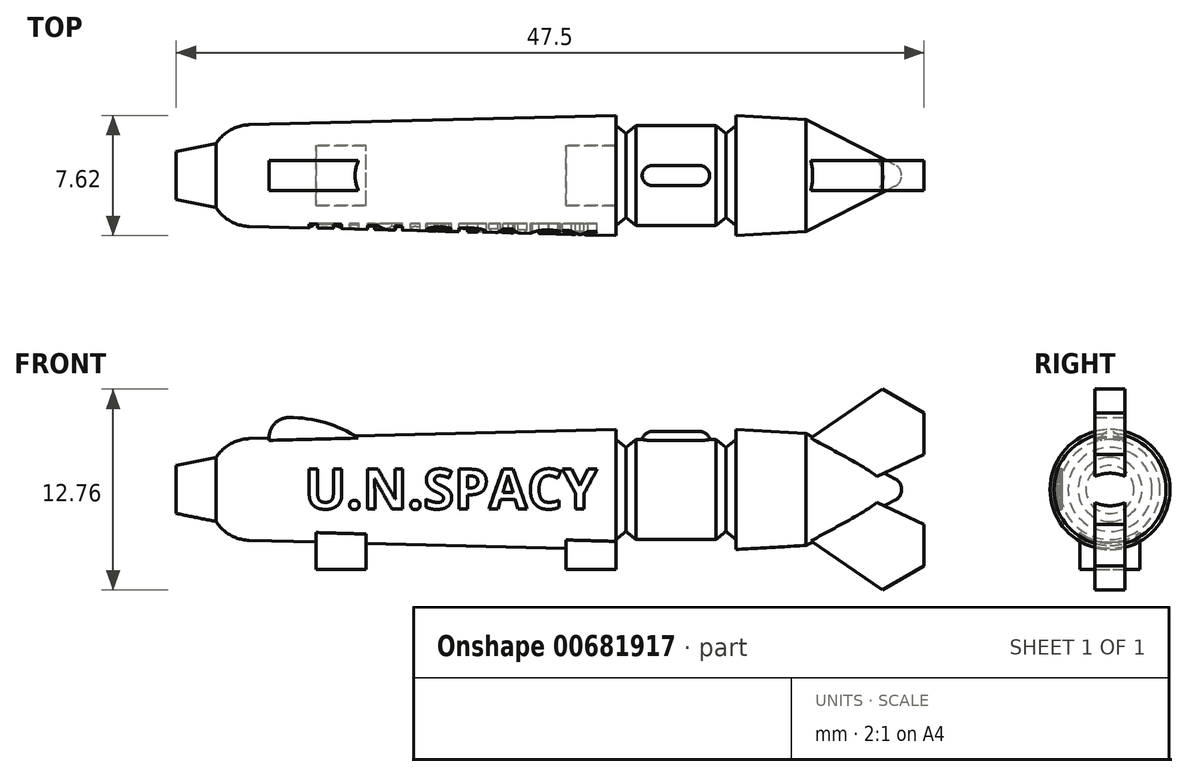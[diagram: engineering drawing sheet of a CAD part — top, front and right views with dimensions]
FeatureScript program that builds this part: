
annotation { "Feature Type Name" : "Feature", "Feature Type Description" : "" }
export const myFeature = defineFeature(function(context is Context, id is Id, definition is map)
    precondition{}
    {
        {
            var Q0;
            Q0=qCreatedBy(makeId("Front.planeOp"),FACE);
            var sketch = newSketch(context, id + "F0", { "sketchPlane" : qUnion([Q0])});
            skLineSegment(sketch, "E0", {"start": v(-36.83, 0) * mm, "end": v(32.69, 0) * mm, "construction": true});
            skLineSegment(sketch, "E1", {"start": v(-27.93, 0) * mm, "end": v(-27.93, 1.52) * mm});
            skLineSegment(sketch, "E2", {"start": v(-27.93, 1.52) * mm, "end": v(-25.4, 2.03) * mm});
            skLineSegment(sketch, "E3", {"start": v(-25.4, 2.03) * mm, "end": v(-25.4, 3.18) * mm});
            skLineSegment(sketch, "E4", {"start": v(-25.4, 3.18) * mm, "end": v(0, 3.81) * mm});
            skLineSegment(sketch, "E5", {"start": v(0, 3.81) * mm, "end": v(0, 3.17) * mm});
            skLineSegment(sketch, "E6", {"start": v(1.27, 3.18) * mm, "end": v(6.35, 3.18) * mm});
            skLineSegment(sketch, "E7", {"start": v(6.99, 2.67) * mm, "end": v(7.62, 3.18) * mm});
            skLineSegment(sketch, "E8", {"start": v(7.62, 3.18) * mm, "end": v(7.62, 3.81) * mm});
            skLineSegment(sketch, "E9", {"start": v(7.62, 3.81) * mm, "end": v(12.07, 3.56) * mm});
            skLineSegment(sketch, "E10", {"start": v(12.07, 3.56) * mm, "end": v(17.73, 0.68) * mm});
            skLineSegment(sketch, "E11", {"start": v(18.14, 0) * mm, "end": v(-27.93, 0) * mm});
            skArc(sketch, "E12", {"start": v(18.14, 0) * mm, "mid": v(18.03, 0.4) * mm, "end": v(17.73, 0.68) * mm});
            skLineSegment(sketch, "E13", {"start": v(6.35, 3.18) * mm, "end": v(6.99, 2.67) * mm});
            skLineSegment(sketch, "E14", {"start": v(3.81, 3.18) * mm, "end": v(3.81, 0) * mm, "construction": true});
            skLineSegment(sketch, "E15.MirrorCS", {"start": v(1.27, 3.18) * mm, "end": v(0.64, 2.67) * mm});
            skLineSegment(sketch, "E16.MirrorCS", {"start": v(0.64, 2.67) * mm, "end": v(0, 3.18) * mm});
            skPoint(sketch, "E17.end.orphan", {"position": v(6.35, 2.16) * mm});
            skPoint(sketch, "E18.orphan", {"position": v(1.27, 2.16) * mm});
            skSolve(sketch);
        }
        {
            var Q0;
            Q0 = qSketchRegion(id + "F0", true);
            var Q1;
            Q1=sQuery(id+"F0.wireOp",EDGE,"E11");
            revolve(context, id + "F1", {"entities" : qUnion([Q0]), "axis" : qUnion([Q1]), "revolveType" : RevolveType.FULL});
        }
        {
            var Q0;
            Q0=makeQuery(id+"F1.opRevolve","SWEPT_EDGE",EDGE,{"disambiguationData":[OSD([sQuery(id+"F0.wireOp",EDGE,"E3"),sQuery(id+"F0.wireOp",EDGE,"E4")])]});
            fillet(context, id + "F2", {"entities" : qUnion([Q0]), "radius" : 2.54 * mm, "allowEdgeOverflow" : false});
        }
        {
            var Q0;
            Q0=qCreatedBy(makeId("Front.planeOp"),FACE);
            var sketch = newSketch(context, id + "F3", { "sketchPlane" : qUnion([Q0])});
            skArc(sketch, "E19", {"start": v(-20.77, 4.57) * mm, "mid": v(-22.03, 3.36) * mm, "end": v(-20.88, 2.04) * mm});
            skArc(sketch, "E20", {"start": v(-14.92, 2.04) * mm, "mid": v(-17.58, 3.92) * mm, "end": v(-20.77, 4.57) * mm});
            skLineSegment(sketch, "E21", {"start": v(-20.88, 2.04) * mm, "end": v(-14.92, 2.04) * mm});
            skPoint(sketch, "E22.orphan", {"position": v(12.68, 0) * mm});
            skLineSegment(sketch, "E23", {"start": v(11.6, 2.73) * mm, "end": v(16.93, 6.38) * mm});
            skLineSegment(sketch, "E24", {"start": v(16.93, 6.38) * mm, "end": v(19.57, 4.86) * mm});
            skLineSegment(sketch, "E25", {"start": v(19.57, 4.86) * mm, "end": v(19.57, 2.23) * mm});
            skLineSegment(sketch, "E26", {"start": v(19.57, 2.23) * mm, "end": v(15.53, 0.34) * mm});
            skLineSegment(sketch, "E27", {"start": v(11.6, 2.73) * mm, "end": v(14.4, 0.34) * mm});
            skLineSegment(sketch, "E28", {"start": v(14.8, 0) * mm, "end": v(12.68, 0) * mm, "construction": true});
            skLineSegment(sketch, "E29.MirrorCS", {"start": v(11.6, -2.73) * mm, "end": v(14.4, -0.34) * mm});
            skLineSegment(sketch, "E30.MirrorCS", {"start": v(11.6, -2.73) * mm, "end": v(16.93, -6.38) * mm});
            skLineSegment(sketch, "E31.MirrorCS", {"start": v(19.57, -4.86) * mm, "end": v(19.57, -2.23) * mm});
            skLineSegment(sketch, "E32.MirrorCS", {"start": v(19.57, -2.23) * mm, "end": v(15.53, -0.34) * mm});
            skLineSegment(sketch, "E33", {"start": v(14.4, 0.34) * mm, "end": v(15.53, 0.34) * mm});
            skPoint(sketch, "E34.MirrorCS.end.orphan", {"position": v(19.57, -4.86) * mm});
            skPoint(sketch, "E34.MirrorCS.start.orphan", {"position": v(16.93, -6.38) * mm});
            skLineSegment(sketch, "E35.MirrorCS", {"start": v(14.4, -0.34) * mm, "end": v(15.53, -0.34) * mm});
            skPoint(sketch, "E36.orphan", {"position": v(14.8, 0) * mm});
            skLineSegment(sketch, "E37.MirrorCS", {"start": v(16.93, -6.38) * mm, "end": v(19.57, -4.86) * mm});
            skSolve(sketch);
        }
        {
            var Q0;
            Q0 = qSketchRegion(id + "F3", true);
            extrude(context, id + "F4", {"entities" : qUnion([Q0]), "operationType" : NewBodyOperationType.ADD, "endBound" : BoundingType.SYMMETRIC, "depth" : 1.9 * mm, "offsetDistance" : 25.4 * mm});
        }
        {
            var Q0;
            Q0=qCreatedBy(makeId("Front.planeOp"),FACE);
            cPlane(context, id + "F5", {"entities" : qUnion([Q0]), "cplaneType" : CPlaneType.OFFSET, "offset" : 3.05 * mm, "width" : 152.4 * mm, "height" : 152.4 * mm});
        }
        {
            var Q0;
            Q0=qCreatedBy(id+"F5.planeOp",FACE);
            var sketch = newSketch(context, id + "F6", { "sketchPlane" : qUnion([Q0])});
            skText(sketch, "E38", { "text": "U.N.SPACY", "fontName": "OpenSans-Bold.ttf"});
            const initialGuessF6  = {"E38": [-0.01978, -0.00123, 1, 0, 0.00254]};
            skSetInitialGuess(sketch, initialGuessF6);
            skSolve(sketch);
        }
        {
            var Q0;
            Q0 = qSketchRegion(id + "F6", true);
            extrude(context, id + "F7", {"entities" : qUnion([Q0]), "operationType" : NewBodyOperationType.REMOVE, "depth" : 25.4 * mm, "offsetDistance" : 25.4 * mm});
        }
        {
            var Q0;
            Q0=qCreatedBy(makeId("Front.planeOp"),FACE);
            var sketch = newSketch(context, id + "F8", { "sketchPlane" : qUnion([Q0])});
            skArc(sketch, "E39", {"start": v(2.29, 3.68) * mm, "mid": v(1.84, 3.5) * mm, "end": v(1.65, 3.05) * mm});
            skLineSegment(sketch, "E40", {"start": v(1.65, 3.05) * mm, "end": v(5.97, 3.05) * mm});
            skLineSegment(sketch, "E41", {"start": v(3.81, 4.43) * mm, "end": v(3.81, -0.67) * mm, "construction": true});
            skArc(sketch, "E42.MirrorC", {"start": v(5.33, 3.68) * mm, "mid": v(5.78, 3.5) * mm, "end": v(5.97, 3.05) * mm});
            skLineSegment(sketch, "E43", {"start": v(2.29, 3.68) * mm, "end": v(5.33, 3.68) * mm});
            skSolve(sketch);
        }
        {
            var Q0;
            Q0=makeQuery(id+"F8.imprint","IMPRINT",FACE,{"disambiguationData":[TD([[makeQuery(id+"F8.imprint","IMPRINT",EDGE,{"derivedFrom":sQuery(id+"F8.wireOp",EDGE,"E39")}),1.0]])]});
            var Q1;
            Q1=sQuery(id+"F8.wireOp",EDGE,"E40");
            revolve(context, id + "F9", {"operationType" : NewBodyOperationType.ADD, "surfaceOperationType" : NewSurfaceOperationType.NEW, "entities" : qUnion([Q0]), "axis" : qUnion([Q1]), "revolveType" : RevolveType.FULL});
        }
        {
            var Q0;
            Q0=qCreatedBy(makeId("Front.planeOp"),FACE);
            var sketch = newSketch(context, id + "F10", { "sketchPlane" : qUnion([Q0])});
            skLineSegment(sketch, "E44", {"start": v(0, -2.54) * mm, "end": v(0, -5.08) * mm});
            skLineSegment(sketch, "E45", {"start": v(0, -5.08) * mm, "end": v(-3.18, -5.08) * mm});
            skLineSegment(sketch, "E46", {"start": v(-3.18, -5.08) * mm, "end": v(-3.18, -2.54) * mm});
            skLineSegment(sketch, "E47", {"start": v(-3.18, -2.54) * mm, "end": v(0, -2.54) * mm});
            skLineSegment(sketch, "E48", {"start": v(-3.18, -5.08) * mm, "end": v(-28.37, -5.08) * mm, "construction": true});
            skLineSegment(sketch, "E49", {"start": v(-15.88, -5.08) * mm, "end": v(-19.05, -5.08) * mm});
            skLineSegment(sketch, "E50", {"start": v(-19.05, -5.08) * mm, "end": v(-19.05, -1.9) * mm});
            skLineSegment(sketch, "E51", {"start": v(-19.05, -1.9) * mm, "end": v(-15.88, -1.9) * mm});
            skLineSegment(sketch, "E52", {"start": v(-15.88, -1.9) * mm, "end": v(-15.88, -5.08) * mm});
            skSolve(sketch);
        }
        {
            var Q0;
            Q0 = qSketchRegion(id + "F10", true);
            extrude(context, id + "F11", {"entities" : qUnion([Q0]), "operationType" : NewBodyOperationType.ADD, "endBound" : BoundingType.SYMMETRIC, "depth" : 3.8 * mm, "offsetDistance" : 25.4 * mm});
        }
    });
